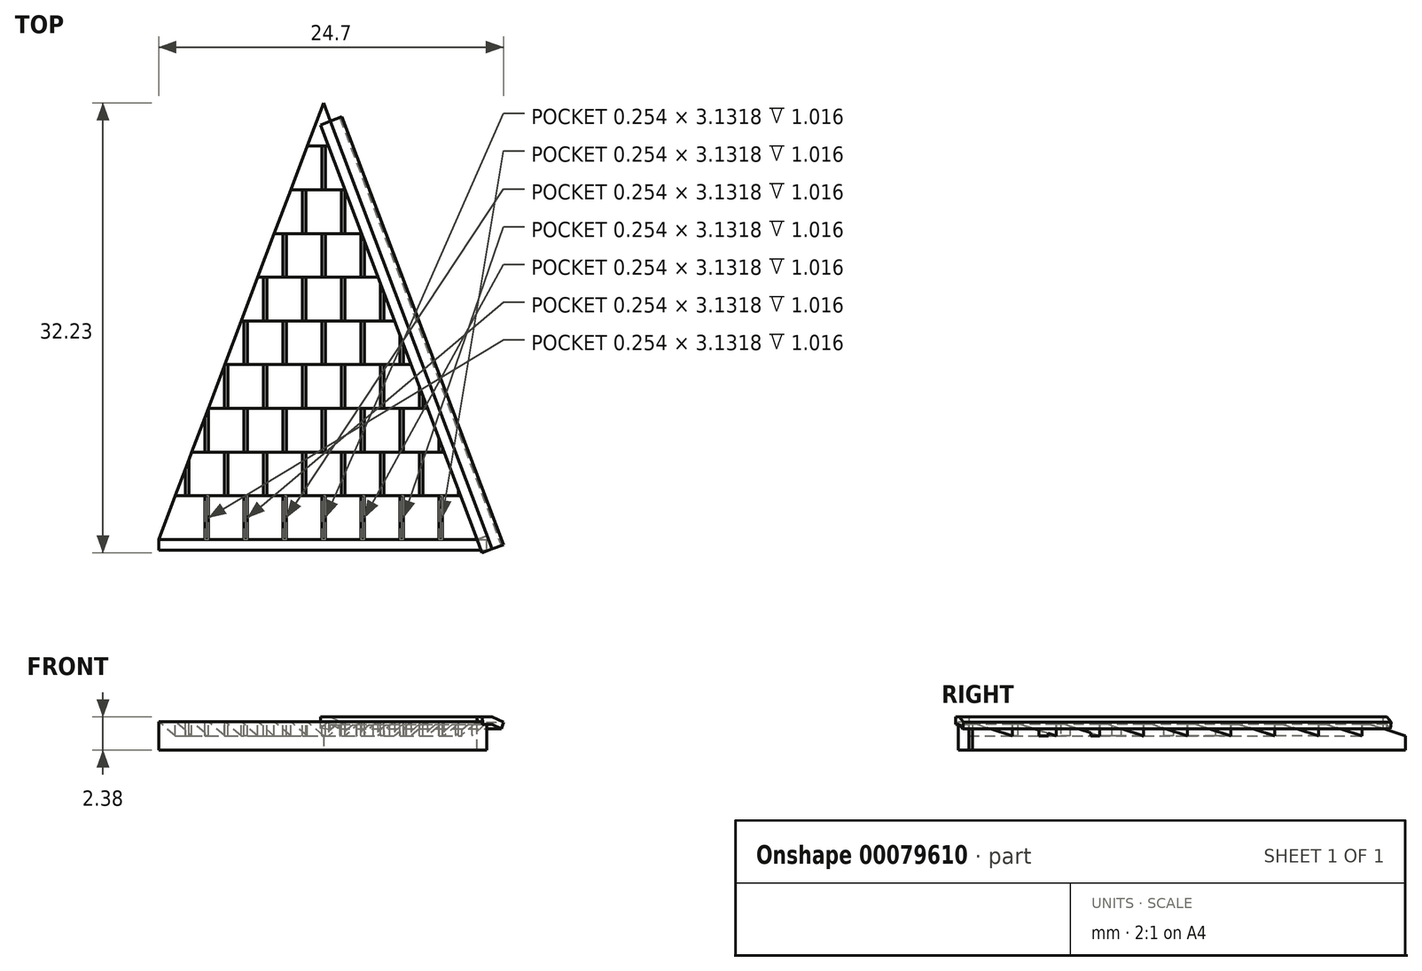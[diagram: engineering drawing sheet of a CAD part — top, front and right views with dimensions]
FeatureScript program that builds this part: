
annotation { "Feature Type Name" : "Feature", "Feature Type Description" : "" }
export const myFeature = defineFeature(function(context is Context, id is Id, definition is map)
    precondition{}
    {
        {
            var Q0;
            Q0=qCreatedBy(makeId("Top.planeOp"),FACE);
            var sketch = newSketch(context, id + "F0", { "sketchPlane" : qUnion([Q0])});
            skLineSegment(sketch, "E0.bottom", {"start": v(-11.8, 0) * mm, "end": v(11.8, 0) * mm});
            skLineSegment(sketch, "E1", {"start": v(-11.8, 0) * mm, "end": v(0, 31.28) * mm});
            skLineSegment(sketch, "E2", {"start": v(0, 31.28) * mm, "end": v(11.8, 0) * mm});
            skPoint(sketch, "E0.right.end.orphan", {"position": v(11.8, 31.28) * mm});
            skPoint(sketch, "E0.left.end.orphan", {"position": v(-11.8, 31.28) * mm});
            skSolve(sketch);
        }
        {
            var Q0;
            Q0 = qSketchRegion(id + "F0", true);
            extrude(context, id + "F1", {"entities" : qUnion([Q0]), "depth" : 2.03 * mm});
        }
        {
            var Q0;
            Q0=qCreatedBy(makeId("Right.planeOp"),FACE);
            var sketch = newSketch(context, id + "F2", { "sketchPlane" : qUnion([Q0])});
            skLineSegment(sketch, "E3", {"start": v(0, 2.03) * mm, "end": v(0, 1.02) * mm});
            skLineSegment(sketch, "E4.1.0.0", {"start": v(3.13, 2.03) * mm, "end": v(3.13, 1.02) * mm});
            skLineSegment(sketch, "E4.2.0.0", {"start": v(6.26, 2.03) * mm, "end": v(6.26, 1.02) * mm});
            skLineSegment(sketch, "E4.3.0.0", {"start": v(9.4, 2.03) * mm, "end": v(9.4, 1.02) * mm});
            skLineSegment(sketch, "E4.4.0.0", {"start": v(12.53, 2.03) * mm, "end": v(12.53, 1.02) * mm});
            skLineSegment(sketch, "E4.5.0.0", {"start": v(15.66, 2.03) * mm, "end": v(15.66, 1.02) * mm});
            skLineSegment(sketch, "E4.6.0.0", {"start": v(18.8, 2.03) * mm, "end": v(18.8, 1.02) * mm});
            skLineSegment(sketch, "E4.7.0.0", {"start": v(21.92, 2.03) * mm, "end": v(21.92, 1.02) * mm});
            skLineSegment(sketch, "E4.8.0.0", {"start": v(25.05, 2.03) * mm, "end": v(25.05, 1.02) * mm});
            skLineSegment(sketch, "E4.9.0.0", {"start": v(28.19, 2.03) * mm, "end": v(28.19, 1.02) * mm});
            skLineSegment(sketch, "E4.direction1", {"start": v(0, 1.02) * mm, "end": v(3.13, 1.02) * mm, "construction": true});
            skLineSegment(sketch, "E5", {"start": v(0, 2.03) * mm, "end": v(3.13, 1.02) * mm});
            skLineSegment(sketch, "E6", {"start": v(3.13, 2.03) * mm, "end": v(6.26, 1.02) * mm});
            skLineSegment(sketch, "E7", {"start": v(6.26, 2.03) * mm, "end": v(9.4, 1.02) * mm});
            skLineSegment(sketch, "E8", {"start": v(9.4, 2.03) * mm, "end": v(12.53, 1.02) * mm});
            skLineSegment(sketch, "E9", {"start": v(12.53, 2.03) * mm, "end": v(15.66, 1.02) * mm});
            skLineSegment(sketch, "E10", {"start": v(15.66, 2.03) * mm, "end": v(18.8, 1.02) * mm});
            skLineSegment(sketch, "E11", {"start": v(18.8, 2.03) * mm, "end": v(21.92, 1.02) * mm});
            skLineSegment(sketch, "E12", {"start": v(21.92, 2.03) * mm, "end": v(25.05, 1.02) * mm});
            skLineSegment(sketch, "E13", {"start": v(25.05, 2.03) * mm, "end": v(28.19, 1.02) * mm});
            skLineSegment(sketch, "E14", {"start": v(0, 2.03) * mm, "end": v(0, 2.92) * mm});
            skLineSegment(sketch, "E15", {"start": v(0, 2.92) * mm, "end": v(28.19, 2.92) * mm});
            skLineSegment(sketch, "E16.0.10.0", {"start": v(31.32, 2.03) * mm, "end": v(31.32, 1.02) * mm});
            skLineSegment(sketch, "E16.0.11.0", {"start": v(34.45, 2.03) * mm, "end": v(34.45, 1.02) * mm});
            skLineSegment(sketch, "E16.0.12.0", {"start": v(37.58, 2.03) * mm, "end": v(37.58, 1.02) * mm});
            skLineSegment(sketch, "E16.0.13.0", {"start": v(40.71, 2.03) * mm, "end": v(40.71, 1.02) * mm});
            skLineSegment(sketch, "E17", {"start": v(28.19, 2.03) * mm, "end": v(31.32, 1.02) * mm});
            skLineSegment(sketch, "E18", {"start": v(31.32, 2.03) * mm, "end": v(31.32, 2.92) * mm});
            skLineSegment(sketch, "E19", {"start": v(31.32, 2.92) * mm, "end": v(28.19, 2.92) * mm});
            skSolve(sketch);
        }
        {
            var Q0;
            Q0 = qSketchRegion(id + "F2", true);
            extrude(context, id + "F3", {"entities" : qUnion([Q0]), "operationType" : NewBodyOperationType.REMOVE, "oppositeDirection" : true, "depth" : 25.4 * mm, "symmetric" : true});
        }
        {
            var Q0;
            Q0=qCreatedBy(makeId("Top.planeOp"),FACE);
            cPlane(context, id + "F4", {"entities" : qUnion([Q0]), "cplaneType" : CPlaneType.OFFSET, "offset" : 2.3 * mm, "width" : 152.4 * mm, "height" : 152.4 * mm});
        }
        {
            var Q0;
            Q0=qCreatedBy(id+"F4.planeOp",FACE);
            var sketch = newSketch(context, id + "F5", { "sketchPlane" : qUnion([Q0])});
            skLineSegment(sketch, "E20.bottom", {"start": v(-0.13, 0) * mm, "end": v(0.13, 0) * mm});
            skLineSegment(sketch, "E20.top", {"start": v(-0.13, 3.13) * mm, "end": v(0.13, 3.13) * mm});
            skLineSegment(sketch, "E20.left", {"start": v(-0.13, 0) * mm, "end": v(-0.13, 3.13) * mm});
            skLineSegment(sketch, "E20.right", {"start": v(0.13, 0) * mm, "end": v(0.13, 3.13) * mm});
            skLineSegment(sketch, "E21.bottom", {"start": v(2.67, 0) * mm, "end": v(2.92, 0) * mm});
            skLineSegment(sketch, "E21.top", {"start": v(2.67, 3.13) * mm, "end": v(2.92, 3.13) * mm});
            skLineSegment(sketch, "E21.left", {"start": v(2.67, 0) * mm, "end": v(2.67, 3.13) * mm});
            skLineSegment(sketch, "E21.right", {"start": v(2.92, 0) * mm, "end": v(2.92, 3.13) * mm});
            skLineSegment(sketch, "E22.bottom", {"start": v(5.46, 0) * mm, "end": v(5.72, 0) * mm});
            skLineSegment(sketch, "E22.top", {"start": v(5.46, 3.13) * mm, "end": v(5.72, 3.13) * mm});
            skLineSegment(sketch, "E22.left", {"start": v(5.46, 0) * mm, "end": v(5.46, 3.13) * mm});
            skLineSegment(sketch, "E22.right", {"start": v(5.72, 0) * mm, "end": v(5.72, 3.13) * mm});
            skLineSegment(sketch, "E23.bottom", {"start": v(-2.92, 0) * mm, "end": v(-2.67, 0) * mm});
            skLineSegment(sketch, "E23.top", {"start": v(-2.92, 3.13) * mm, "end": v(-2.67, 3.13) * mm});
            skLineSegment(sketch, "E23.left", {"start": v(-2.92, 0) * mm, "end": v(-2.92, 3.13) * mm});
            skLineSegment(sketch, "E23.right", {"start": v(-2.67, 0) * mm, "end": v(-2.67, 3.13) * mm});
            skLineSegment(sketch, "E24.bottom", {"start": v(8.26, 0) * mm, "end": v(8.5, 0) * mm});
            skLineSegment(sketch, "E24.top", {"start": v(8.26, 3.13) * mm, "end": v(8.5, 3.13) * mm});
            skLineSegment(sketch, "E24.left", {"start": v(8.26, 0) * mm, "end": v(8.26, 3.13) * mm});
            skLineSegment(sketch, "E24.right", {"start": v(8.5, 0) * mm, "end": v(8.5, 3.13) * mm});
            skLineSegment(sketch, "E25.bottom", {"start": v(-5.46, 0) * mm, "end": v(-5.72, 0) * mm});
            skLineSegment(sketch, "E25.top", {"start": v(-5.46, 3.13) * mm, "end": v(-5.72, 3.13) * mm});
            skLineSegment(sketch, "E25.left", {"start": v(-5.46, 0) * mm, "end": v(-5.46, 3.13) * mm});
            skLineSegment(sketch, "E25.right", {"start": v(-5.72, 0) * mm, "end": v(-5.72, 3.13) * mm});
            skLineSegment(sketch, "E26.bottom", {"start": v(-8.26, 0) * mm, "end": v(-8.5, 0) * mm});
            skLineSegment(sketch, "E26.top", {"start": v(-8.26, 3.13) * mm, "end": v(-8.5, 3.13) * mm});
            skLineSegment(sketch, "E26.left", {"start": v(-8.26, 0) * mm, "end": v(-8.26, 3.13) * mm});
            skLineSegment(sketch, "E26.right", {"start": v(-8.5, 0) * mm, "end": v(-8.5, 3.13) * mm});
            skLineSegment(sketch, "E27.1.0.0", {"start": v(2.67, 6.26) * mm, "end": v(2.67, 9.4) * mm});
            skLineSegment(sketch, "E27.1.0.1", {"start": v(-5.46, 6.26) * mm, "end": v(-5.46, 9.4) * mm});
            skLineSegment(sketch, "E27.1.0.2", {"start": v(5.46, 6.26) * mm, "end": v(5.46, 9.4) * mm});
            skLineSegment(sketch, "E27.1.0.3", {"start": v(5.72, 6.26) * mm, "end": v(5.72, 9.4) * mm});
            skLineSegment(sketch, "E27.1.0.4", {"start": v(0.13, 6.26) * mm, "end": v(0.13, 9.4) * mm});
            skLineSegment(sketch, "E27.1.0.5", {"start": v(-0.13, 6.26) * mm, "end": v(-0.13, 9.4) * mm});
            skLineSegment(sketch, "E27.1.0.6", {"start": v(2.92, 6.26) * mm, "end": v(2.92, 9.4) * mm});
            skLineSegment(sketch, "E27.1.0.7", {"start": v(-2.67, 6.26) * mm, "end": v(-2.67, 9.4) * mm});
            skLineSegment(sketch, "E27.1.0.8", {"start": v(-2.92, 6.26) * mm, "end": v(-2.92, 9.4) * mm});
            skLineSegment(sketch, "E27.1.0.9", {"start": v(8.5, 6.26) * mm, "end": v(8.5, 9.4) * mm});
            skLineSegment(sketch, "E27.1.0.10", {"start": v(8.26, 6.26) * mm, "end": v(8.26, 9.4) * mm});
            skLineSegment(sketch, "E27.1.0.11", {"start": v(-5.71, 6.26) * mm, "end": v(-5.71, 9.4) * mm});
            skLineSegment(sketch, "E27.1.0.12", {"start": v(2.67, 6.26) * mm, "end": v(2.92, 6.26) * mm});
            skLineSegment(sketch, "E27.1.0.13", {"start": v(2.67, 9.4) * mm, "end": v(2.92, 9.4) * mm});
            skLineSegment(sketch, "E27.1.0.14", {"start": v(5.46, 6.26) * mm, "end": v(5.71, 6.26) * mm});
            skLineSegment(sketch, "E27.1.0.15", {"start": v(-5.46, 6.26) * mm, "end": v(-5.71, 6.26) * mm});
            skLineSegment(sketch, "E27.1.0.16", {"start": v(5.46, 9.4) * mm, "end": v(5.72, 9.4) * mm});
            skLineSegment(sketch, "E27.1.0.17", {"start": v(-2.92, 6.26) * mm, "end": v(-2.67, 6.26) * mm});
            skLineSegment(sketch, "E27.1.0.18", {"start": v(-2.92, 9.4) * mm, "end": v(-2.67, 9.4) * mm});
            skLineSegment(sketch, "E27.1.0.19", {"start": v(-5.46, 9.4) * mm, "end": v(-5.71, 9.4) * mm});
            skLineSegment(sketch, "E27.1.0.20", {"start": v(-0.13, 9.4) * mm, "end": v(0.13, 9.4) * mm});
            skLineSegment(sketch, "E27.1.0.21", {"start": v(-0.13, 6.26) * mm, "end": v(0.13, 6.26) * mm});
            skLineSegment(sketch, "E27.1.0.22", {"start": v(8.26, 9.4) * mm, "end": v(8.5, 9.4) * mm});
            skLineSegment(sketch, "E27.1.0.23", {"start": v(8.26, 6.26) * mm, "end": v(8.5, 6.26) * mm});
            skLineSegment(sketch, "E27.2.0.0", {"start": v(2.67, 12.53) * mm, "end": v(2.67, 15.66) * mm});
            skLineSegment(sketch, "E27.2.0.2", {"start": v(5.46, 12.53) * mm, "end": v(5.46, 15.66) * mm});
            skLineSegment(sketch, "E27.2.0.3", {"start": v(5.72, 12.53) * mm, "end": v(5.72, 15.66) * mm});
            skLineSegment(sketch, "E27.2.0.4", {"start": v(0.13, 12.53) * mm, "end": v(0.13, 15.66) * mm});
            skLineSegment(sketch, "E27.2.0.5", {"start": v(-0.13, 12.53) * mm, "end": v(-0.13, 15.66) * mm});
            skLineSegment(sketch, "E27.2.0.6", {"start": v(2.92, 12.53) * mm, "end": v(2.92, 15.66) * mm});
            skLineSegment(sketch, "E27.2.0.7", {"start": v(-2.67, 12.53) * mm, "end": v(-2.67, 15.66) * mm});
            skLineSegment(sketch, "E27.2.0.8", {"start": v(-2.92, 12.53) * mm, "end": v(-2.92, 15.66) * mm});
            skLineSegment(sketch, "E27.2.0.12", {"start": v(2.67, 12.53) * mm, "end": v(2.92, 12.53) * mm});
            skLineSegment(sketch, "E27.2.0.13", {"start": v(2.67, 15.66) * mm, "end": v(2.92, 15.66) * mm});
            skLineSegment(sketch, "E27.2.0.14", {"start": v(5.46, 12.53) * mm, "end": v(5.72, 12.53) * mm});
            skLineSegment(sketch, "E27.2.0.16", {"start": v(5.46, 15.66) * mm, "end": v(5.71, 15.66) * mm});
            skLineSegment(sketch, "E27.2.0.17", {"start": v(-2.92, 12.53) * mm, "end": v(-2.67, 12.53) * mm});
            skLineSegment(sketch, "E27.2.0.18", {"start": v(-2.92, 15.66) * mm, "end": v(-2.67, 15.66) * mm});
            skLineSegment(sketch, "E27.2.0.20", {"start": v(-0.13, 15.66) * mm, "end": v(0.13, 15.66) * mm});
            skLineSegment(sketch, "E27.2.0.21", {"start": v(-0.13, 12.53) * mm, "end": v(0.13, 12.53) * mm});
            skLineSegment(sketch, "E27.direction1", {"start": v(2.67, 0) * mm, "end": v(2.67, 6.26) * mm, "construction": true});
            skLineSegment(sketch, "E28.0.3.0", {"start": v(2.67, 18.8) * mm, "end": v(2.67, 21.92) * mm});
            skLineSegment(sketch, "E28.12.3.0", {"start": v(0.13, 18.8) * mm, "end": v(0.13, 21.92) * mm});
            skLineSegment(sketch, "E28.15.3.0", {"start": v(-0.13, 18.8) * mm, "end": v(-0.13, 21.92) * mm});
            skLineSegment(sketch, "E28.18.3.0", {"start": v(2.92, 18.8) * mm, "end": v(2.92, 21.92) * mm});
            skLineSegment(sketch, "E28.21.3.0", {"start": v(-2.67, 18.8) * mm, "end": v(-2.67, 21.92) * mm});
            skLineSegment(sketch, "E28.24.3.0", {"start": v(-2.92, 18.8) * mm, "end": v(-2.92, 21.92) * mm});
            skLineSegment(sketch, "E28.36.3.0", {"start": v(2.67, 18.8) * mm, "end": v(2.92, 18.8) * mm});
            skLineSegment(sketch, "E28.39.3.0", {"start": v(2.67, 21.92) * mm, "end": v(2.92, 21.92) * mm});
            skLineSegment(sketch, "E28.51.3.0", {"start": v(-2.92, 18.8) * mm, "end": v(-2.67, 18.8) * mm});
            skLineSegment(sketch, "E28.54.3.0", {"start": v(-2.92, 21.92) * mm, "end": v(-2.67, 21.92) * mm});
            skLineSegment(sketch, "E28.60.3.0", {"start": v(-0.13, 21.92) * mm, "end": v(0.13, 21.92) * mm});
            skLineSegment(sketch, "E28.63.3.0", {"start": v(-0.13, 18.8) * mm, "end": v(0.13, 18.8) * mm});
            skLineSegment(sketch, "E29.12.4.0", {"start": v(0.13, 25.05) * mm, "end": v(0.13, 28.19) * mm});
            skLineSegment(sketch, "E29.15.4.0", {"start": v(-0.13, 25.05) * mm, "end": v(-0.13, 28.19) * mm});
            skLineSegment(sketch, "E29.60.4.0", {"start": v(-0.13, 28.19) * mm, "end": v(0.13, 28.19) * mm});
            skLineSegment(sketch, "E29.63.4.0", {"start": v(-0.13, 25.05) * mm, "end": v(0.13, 25.05) * mm});
            skLineSegment(sketch, "E30.bottom", {"start": v(-8.26, 6.26) * mm, "end": v(-8.5, 6.26) * mm});
            skLineSegment(sketch, "E30.top", {"start": v(-8.26, 9.4) * mm, "end": v(-8.5, 9.4) * mm});
            skLineSegment(sketch, "E30.left", {"start": v(-8.26, 6.26) * mm, "end": v(-8.26, 9.4) * mm});
            skLineSegment(sketch, "E30.right", {"start": v(-8.5, 6.26) * mm, "end": v(-8.5, 9.4) * mm});
            skLineSegment(sketch, "E31.bottom", {"start": v(-5.46, 12.53) * mm, "end": v(-5.72, 12.53) * mm});
            skLineSegment(sketch, "E31.top", {"start": v(-5.46, 15.66) * mm, "end": v(-5.72, 15.66) * mm});
            skLineSegment(sketch, "E31.left", {"start": v(-5.46, 12.53) * mm, "end": v(-5.46, 15.66) * mm});
            skLineSegment(sketch, "E31.right", {"start": v(-5.72, 12.53) * mm, "end": v(-5.72, 15.66) * mm});
            skLineSegment(sketch, "E32.bottom", {"start": v(1.27, 6.26) * mm, "end": v(1.52, 6.26) * mm});
            skLineSegment(sketch, "E32.top", {"start": v(1.27, 3.13) * mm, "end": v(1.52, 3.13) * mm});
            skLineSegment(sketch, "E32.left", {"start": v(1.27, 6.26) * mm, "end": v(1.27, 3.13) * mm});
            skLineSegment(sketch, "E32.right", {"start": v(1.52, 6.26) * mm, "end": v(1.52, 3.13) * mm});
            skLineSegment(sketch, "E33.bottom", {"start": v(-1.52, 6.26) * mm, "end": v(-1.27, 6.26) * mm});
            skLineSegment(sketch, "E33.top", {"start": v(-1.52, 3.13) * mm, "end": v(-1.27, 3.13) * mm});
            skLineSegment(sketch, "E33.left", {"start": v(-1.52, 6.26) * mm, "end": v(-1.52, 3.13) * mm});
            skLineSegment(sketch, "E33.right", {"start": v(-1.27, 6.26) * mm, "end": v(-1.27, 3.13) * mm});
            skLineSegment(sketch, "E34.bottom", {"start": v(-4.32, 6.26) * mm, "end": v(-4.06, 6.26) * mm});
            skLineSegment(sketch, "E34.top", {"start": v(-4.32, 3.13) * mm, "end": v(-4.06, 3.13) * mm});
            skLineSegment(sketch, "E34.left", {"start": v(-4.32, 6.26) * mm, "end": v(-4.32, 3.13) * mm});
            skLineSegment(sketch, "E34.right", {"start": v(-4.06, 6.26) * mm, "end": v(-4.06, 3.13) * mm});
            skLineSegment(sketch, "E35.bottom", {"start": v(-7.11, 6.26) * mm, "end": v(-6.86, 6.26) * mm});
            skLineSegment(sketch, "E35.top", {"start": v(-7.11, 3.13) * mm, "end": v(-6.86, 3.13) * mm});
            skLineSegment(sketch, "E35.left", {"start": v(-7.11, 6.26) * mm, "end": v(-7.11, 3.13) * mm});
            skLineSegment(sketch, "E35.right", {"start": v(-6.86, 6.26) * mm, "end": v(-6.86, 3.13) * mm});
            skLineSegment(sketch, "E36.bottom", {"start": v(-9.65, 3.13) * mm, "end": v(-9.9, 3.13) * mm});
            skLineSegment(sketch, "E36.top", {"start": v(-9.65, 6.26) * mm, "end": v(-9.9, 6.26) * mm});
            skLineSegment(sketch, "E36.left", {"start": v(-9.65, 3.13) * mm, "end": v(-9.65, 6.26) * mm});
            skLineSegment(sketch, "E36.right", {"start": v(-9.9, 3.13) * mm, "end": v(-9.9, 6.26) * mm});
            skLineSegment(sketch, "E37.bottom", {"start": v(4.32, 3.13) * mm, "end": v(4.06, 3.13) * mm});
            skLineSegment(sketch, "E37.top", {"start": v(4.32, 6.26) * mm, "end": v(4.06, 6.26) * mm});
            skLineSegment(sketch, "E37.left", {"start": v(4.32, 3.13) * mm, "end": v(4.32, 6.26) * mm});
            skLineSegment(sketch, "E37.right", {"start": v(4.06, 3.13) * mm, "end": v(4.06, 6.26) * mm});
            skLineSegment(sketch, "E38.bottom", {"start": v(6.86, 6.26) * mm, "end": v(7.11, 6.26) * mm});
            skLineSegment(sketch, "E38.top", {"start": v(6.86, 3.13) * mm, "end": v(7.11, 3.13) * mm});
            skLineSegment(sketch, "E38.left", {"start": v(6.86, 6.26) * mm, "end": v(6.86, 3.13) * mm});
            skLineSegment(sketch, "E38.right", {"start": v(7.11, 6.26) * mm, "end": v(7.11, 3.13) * mm});
            skLineSegment(sketch, "E39.bottom", {"start": v(9.65, 6.26) * mm, "end": v(9.9, 6.26) * mm});
            skLineSegment(sketch, "E39.top", {"start": v(9.65, 3.13) * mm, "end": v(9.9, 3.13) * mm});
            skLineSegment(sketch, "E39.left", {"start": v(9.65, 6.26) * mm, "end": v(9.65, 3.13) * mm});
            skLineSegment(sketch, "E39.right", {"start": v(9.9, 6.26) * mm, "end": v(9.9, 3.13) * mm});
            skLineSegment(sketch, "E40.1.0.0", {"start": v(-7.11, 12.53) * mm, "end": v(-7.11, 9.4) * mm});
            skLineSegment(sketch, "E40.1.0.1", {"start": v(-6.86, 12.53) * mm, "end": v(-6.86, 9.4) * mm});
            skLineSegment(sketch, "E40.1.0.2", {"start": v(-7.11, 9.4) * mm, "end": v(-6.86, 9.4) * mm});
            skLineSegment(sketch, "E40.1.0.3", {"start": v(-7.11, 12.53) * mm, "end": v(-6.86, 12.53) * mm});
            skLineSegment(sketch, "E40.1.0.4", {"start": v(-4.32, 12.53) * mm, "end": v(-4.32, 9.4) * mm});
            skLineSegment(sketch, "E40.1.0.5", {"start": v(-4.32, 9.4) * mm, "end": v(-4.06, 9.4) * mm});
            skLineSegment(sketch, "E40.1.0.6", {"start": v(-4.32, 12.53) * mm, "end": v(-4.06, 12.53) * mm});
            skLineSegment(sketch, "E40.1.0.7", {"start": v(-4.06, 12.53) * mm, "end": v(-4.06, 9.4) * mm});
            skLineSegment(sketch, "E40.1.0.8", {"start": v(-1.27, 12.53) * mm, "end": v(-1.27, 9.4) * mm});
            skLineSegment(sketch, "E40.1.0.9", {"start": v(-1.52, 12.53) * mm, "end": v(-1.52, 9.4) * mm});
            skLineSegment(sketch, "E40.1.0.10", {"start": v(-1.52, 9.4) * mm, "end": v(-1.27, 9.4) * mm});
            skLineSegment(sketch, "E40.1.0.11", {"start": v(-1.52, 12.53) * mm, "end": v(-1.27, 12.53) * mm});
            skLineSegment(sketch, "E40.1.0.12", {"start": v(1.52, 12.53) * mm, "end": v(1.52, 9.4) * mm});
            skLineSegment(sketch, "E40.1.0.13", {"start": v(1.27, 12.53) * mm, "end": v(1.27, 9.4) * mm});
            skLineSegment(sketch, "E40.1.0.14", {"start": v(1.27, 9.4) * mm, "end": v(1.52, 9.4) * mm});
            skLineSegment(sketch, "E40.1.0.15", {"start": v(1.27, 12.53) * mm, "end": v(1.52, 12.53) * mm});
            skLineSegment(sketch, "E40.1.0.16", {"start": v(4.32, 9.4) * mm, "end": v(4.32, 12.53) * mm});
            skLineSegment(sketch, "E40.1.0.17", {"start": v(4.06, 9.4) * mm, "end": v(4.06, 12.53) * mm});
            skLineSegment(sketch, "E40.1.0.18", {"start": v(4.32, 9.4) * mm, "end": v(4.06, 9.4) * mm});
            skLineSegment(sketch, "E40.1.0.19", {"start": v(4.32, 12.53) * mm, "end": v(4.06, 12.53) * mm});
            skLineSegment(sketch, "E40.1.0.20", {"start": v(6.86, 9.4) * mm, "end": v(7.11, 9.4) * mm});
            skLineSegment(sketch, "E40.1.0.21", {"start": v(6.86, 12.53) * mm, "end": v(6.86, 9.4) * mm});
            skLineSegment(sketch, "E40.1.0.22", {"start": v(7.11, 12.53) * mm, "end": v(7.11, 9.4) * mm});
            skLineSegment(sketch, "E40.1.0.23", {"start": v(6.86, 12.53) * mm, "end": v(7.11, 12.53) * mm});
            skLineSegment(sketch, "E40.2.0.4", {"start": v(-4.32, 18.8) * mm, "end": v(-4.32, 15.66) * mm});
            skLineSegment(sketch, "E40.2.0.5", {"start": v(-4.32, 15.66) * mm, "end": v(-4.06, 15.66) * mm});
            skLineSegment(sketch, "E40.2.0.6", {"start": v(-4.32, 18.8) * mm, "end": v(-4.06, 18.8) * mm});
            skLineSegment(sketch, "E40.2.0.7", {"start": v(-4.06, 18.8) * mm, "end": v(-4.06, 15.66) * mm});
            skLineSegment(sketch, "E40.2.0.8", {"start": v(-1.27, 18.8) * mm, "end": v(-1.27, 15.66) * mm});
            skLineSegment(sketch, "E40.2.0.9", {"start": v(-1.52, 18.8) * mm, "end": v(-1.52, 15.66) * mm});
            skLineSegment(sketch, "E40.2.0.10", {"start": v(-1.52, 15.66) * mm, "end": v(-1.27, 15.66) * mm});
            skLineSegment(sketch, "E40.2.0.11", {"start": v(-1.52, 18.8) * mm, "end": v(-1.27, 18.8) * mm});
            skLineSegment(sketch, "E40.2.0.12", {"start": v(1.52, 18.8) * mm, "end": v(1.52, 15.66) * mm});
            skLineSegment(sketch, "E40.2.0.13", {"start": v(1.27, 18.8) * mm, "end": v(1.27, 15.66) * mm});
            skLineSegment(sketch, "E40.2.0.14", {"start": v(1.27, 15.66) * mm, "end": v(1.52, 15.66) * mm});
            skLineSegment(sketch, "E40.2.0.15", {"start": v(1.27, 18.8) * mm, "end": v(1.52, 18.8) * mm});
            skLineSegment(sketch, "E40.2.0.16", {"start": v(4.32, 15.66) * mm, "end": v(4.32, 18.8) * mm});
            skLineSegment(sketch, "E40.2.0.17", {"start": v(4.06, 15.66) * mm, "end": v(4.06, 18.8) * mm});
            skLineSegment(sketch, "E40.2.0.18", {"start": v(4.32, 15.66) * mm, "end": v(4.06, 15.66) * mm});
            skLineSegment(sketch, "E40.2.0.19", {"start": v(4.32, 18.8) * mm, "end": v(4.06, 18.8) * mm});
            skLineSegment(sketch, "E40.3.0.8", {"start": v(-1.27, 25.05) * mm, "end": v(-1.27, 21.92) * mm});
            skLineSegment(sketch, "E40.3.0.9", {"start": v(-1.52, 25.05) * mm, "end": v(-1.52, 21.92) * mm});
            skLineSegment(sketch, "E40.3.0.10", {"start": v(-1.52, 21.92) * mm, "end": v(-1.27, 21.92) * mm});
            skLineSegment(sketch, "E40.3.0.11", {"start": v(-1.52, 25.05) * mm, "end": v(-1.27, 25.05) * mm});
            skLineSegment(sketch, "E40.3.0.12", {"start": v(1.52, 25.05) * mm, "end": v(1.52, 21.92) * mm});
            skLineSegment(sketch, "E40.3.0.13", {"start": v(1.27, 25.05) * mm, "end": v(1.27, 21.92) * mm});
            skLineSegment(sketch, "E40.3.0.14", {"start": v(1.27, 21.92) * mm, "end": v(1.52, 21.92) * mm});
            skLineSegment(sketch, "E40.3.0.15", {"start": v(1.27, 25.05) * mm, "end": v(1.52, 25.05) * mm});
            skLineSegment(sketch, "E40.direction1", {"start": v(-7.11, 3.13) * mm, "end": v(-7.11, 9.4) * mm, "construction": true});
            skSolve(sketch);
        }
        {
            var Q0;
            Q0 = qSketchRegion(id + "F5", true);
            extrude(context, id + "F6", {"entities" : qUnion([Q0]), "operationType" : NewBodyOperationType.REMOVE, "oppositeDirection" : true, "depth" : 1.27 * mm});
        }
        {
            var Q0;
            Q0=qCreatedBy(id+"F4.planeOp",FACE);
            var sketch = newSketch(context, id + "F7", { "sketchPlane" : qUnion([Q0])});
            skLineSegment(sketch, "E41", {"start": v(11, 0) * mm, "end": v(12.42, 0.54) * mm});
            skLineSegment(sketch, "E42", {"start": v(11, 0) * mm, "end": v(11.26, -0.7) * mm});
            skLineSegment(sketch, "E43", {"start": v(11.26, -0.7) * mm, "end": v(12.71, -0.16) * mm});
            skLineSegment(sketch, "E44", {"start": v(12.71, -0.16) * mm, "end": v(12.42, 0.54) * mm});
            skSolve(sketch);
        }
        {
            var Q0;
            Q0 = qSketchRegion(id + "F7", true);
            extrude(context, id + "F8", {"entities" : qUnion([Q0]), "operationType" : NewBodyOperationType.REMOVE, "oppositeDirection" : true, "depth" : 25.4 * mm});
        }
        {
            var Q0;
            Q0=makeQuery(id+"F8.boolean.opBoolean","COPY",FACE,{"derivedFrom":makeQuery(id+"F8.opExtrude","SWEPT_FACE",FACE,{"disambiguationData":[OSD([sQuery(id+"F7.wireOp",EDGE,"E41")])]})});
            var sketch = newSketch(context, id + "F9", { "sketchPlane" : qUnion([Q0])});
            skLineSegment(sketch, "E45", {"start": v(10.28, 2.38) * mm, "end": v(11.05, 2.38) * mm});
            skLineSegment(sketch, "E46", {"start": v(11.76, 1.52) * mm, "end": v(11.05, 1.83) * mm});
            skLineSegment(sketch, "E47", {"start": v(11.05, 1.83) * mm, "end": v(10.36, 1.83) * mm});
            skLineSegment(sketch, "E48", {"start": v(11.05, 2.38) * mm, "end": v(11.92, 2) * mm});
            skLineSegment(sketch, "E49", {"start": v(11.92, 2) * mm, "end": v(11.76, 1.52) * mm});
            skLineSegment(sketch, "E50", {"start": v(10.28, 2.38) * mm, "end": v(10.36, 1.83) * mm});
            skSolve(sketch);
        }
        {
            var Q0;
            Q0 = qSketchRegion(id + "F9", true);
            extrude(context, id + "F10", {"entities" : qUnion([Q0]), "operationType" : NewBodyOperationType.ADD, "oppositeDirection" : true, "depth" : 31.75 * mm, "hasSecondDirection" : true, "secondDirectionOppositeDirection" : false, "secondDirectionDepth" : 1.02 * mm});
        }
        {
            var Q0;
            Q0=makeQuery(id+"F1.opExtrude","SWEPT_FACE",FACE,{"disambiguationData":[OSD([sQuery(id+"F0.wireOp",EDGE,"E0.bottom")])]});
            var sketch = newSketch(context, id + "F11", { "sketchPlane" : qUnion([Q0])});
            skLineSegment(sketch, "E51.bottom", {"start": v(-11.8, 2.03) * mm, "end": v(11.7, 2.03) * mm});
            skLineSegment(sketch, "E51.top", {"start": v(-11.8, 0) * mm, "end": v(11.7, 0) * mm});
            skLineSegment(sketch, "E51.left", {"start": v(-11.8, 2.03) * mm, "end": v(-11.8, 0) * mm});
            skLineSegment(sketch, "E51.right", {"start": v(11.7, 2.03) * mm, "end": v(11.7, 0) * mm});
            skSolve(sketch);
        }
        {
            var Q0;
            Q0 = qSketchRegion(id + "F11", true);
            extrude(context, id + "F12", {"entities" : qUnion([Q0]), "operationType" : NewBodyOperationType.ADD, "depth" : 0.76 * mm});
        }
        {
            var Q0;
            Q0=makeQuery(id+"F10.opExtrude","SWEPT_FACE",FACE,{"disambiguationData":[OSD([sQuery(id+"F9.wireOp",EDGE,"E45")])]});
            var sketch = newSketch(context, id + "F13", { "sketchPlane" : qUnion([Q0])});
            skLineSegment(sketch, "E52", {"start": v(-0.23, 29.7) * mm, "end": v(0.48, 29.97) * mm});
            skLineSegment(sketch, "E53", {"start": v(0.48, 29.97) * mm, "end": v(11.69, 0.32) * mm});
            skLineSegment(sketch, "E54", {"start": v(-0.23, 29.7) * mm, "end": v(10.98, 0.04) * mm});
            skLineSegment(sketch, "E55", {"start": v(10.98, 0.04) * mm, "end": v(11.69, 0.32) * mm});
            skSolve(sketch);
        }
        {
            var Q0;
            Q0 = qSketchRegion(id + "F13", true);
            var Q1;
            Q1=makeQuery(id+"F12.boolean.opBoolean","MERGE",FACE,{"derivedFrom":[makeQuery(id+"F1.opExtrude","CAP_FACE",FACE,{"disambiguationData":[OSD([sQuery(id+"F0.wireOp",EDGE,"E0.bottom"),sQuery(id+"F0.wireOp",EDGE,"E1"),sQuery(id+"F0.wireOp",EDGE,"E2")])],"isStart":true}),makeQuery(id+"F12.opExtrude","SWEPT_FACE",FACE,{"disambiguationData":[OSD([sQuery(id+"F11.wireOp",EDGE,"E51.top")])]})]});
            extrude(context, id + "F14", {"entities" : qUnion([Q0]), "operationType" : NewBodyOperationType.ADD, "endBound" : BoundingType.UP_TO_SURFACE, "oppositeDirection" : true, "endBoundEntityFace" : qUnion([Q1]), "depth" : 25.4 * mm});
        }
    });
